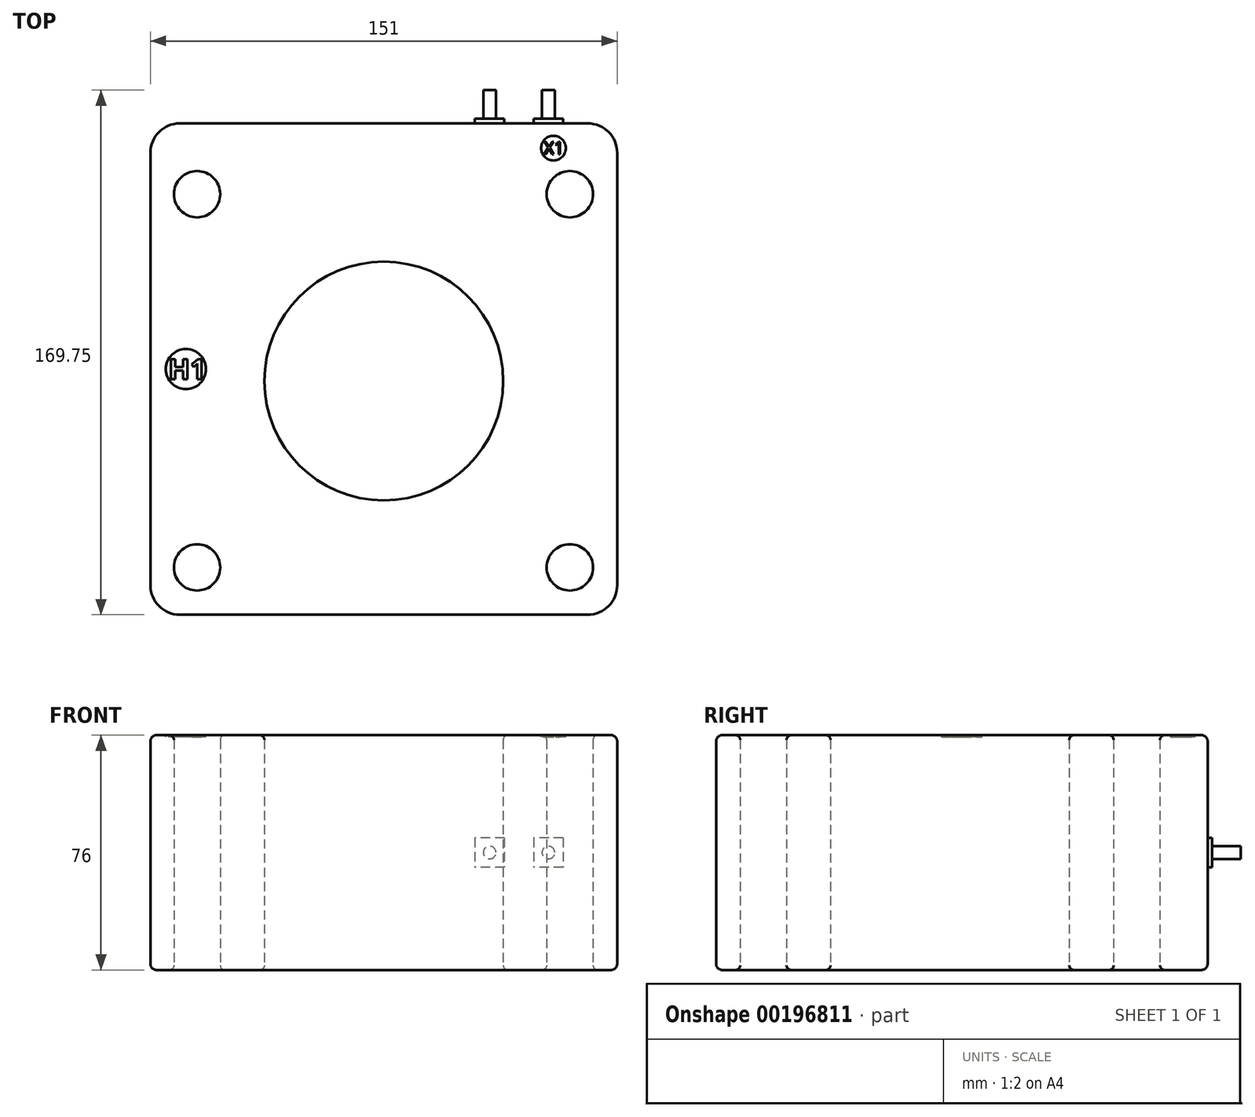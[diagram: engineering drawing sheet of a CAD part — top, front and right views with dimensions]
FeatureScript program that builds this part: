
annotation { "Feature Type Name" : "Feature", "Feature Type Description" : "" }
export const myFeature = defineFeature(function(context is Context, id is Id, definition is map)
    precondition{}
    {
        {
            var Q0;
            Q0=qCreatedBy(makeId("Top.planeOp"),FACE);
            var sketch = newSketch(context, id + "F0", { "sketchPlane" : qUnion([Q0])});
            skLineSegment(sketch, "E0.bottom", {"start": v(75.5, -79.5) * mm, "end": v(-75.5, -79.5) * mm});
            skLineSegment(sketch, "E0.top", {"start": v(75.5, 79.5) * mm, "end": v(-75.5, 79.5) * mm});
            skLineSegment(sketch, "E0.left", {"start": v(75.5, -79.5) * mm, "end": v(75.5, 79.5) * mm});
            skLineSegment(sketch, "E0.right", {"start": v(-75.5, -79.5) * mm, "end": v(-75.5, 79.5) * mm});
            skPoint(sketch, "E0.middle", {"position": v(0, 0) * mm});
            skCircle(sketch, "E1", {"center": v(0, -3.88) * mm, "radius": 38.62 * mm});
            skCircle(sketch, "E2", {"center": v(-60.4, 56.6) * mm, "radius": 7.5 * mm});
            skCircle(sketch, "E3", {"center": v(60.2, 56.6) * mm, "radius": 7.5 * mm});
            skCircle(sketch, "E4", {"center": v(-60.4, -64.2) * mm, "radius": 7.5 * mm});
            skCircle(sketch, "E5", {"center": v(60.2, -64.2) * mm, "radius": 7.5 * mm});
            skSolve(sketch);
        }
        {
            var Q0;
            Q0=makeQuery(id+"F0.imprint","IMPRINT",FACE,{"disambiguationData":[TD([[makeQuery(id+"F0.imprint","IMPRINT",EDGE,{"derivedFrom":sQuery(id+"F0.wireOp",EDGE,"E0.bottom")}),-1.0]])]});
            extrude(context, id + "F1", {"entities" : qUnion([Q0]), "depth" : 76 * mm});
        }
        {
            var Q0;
            Q0=makeQuery(id+"F1.opExtrude","SWEPT_FACE",FACE,{"disambiguationData":[OSD([sQuery(id+"F0.wireOp",EDGE,"E0.top")])]});
            var sketch = newSketch(context, id + "F2", { "sketchPlane" : qUnion([Q0])});
            skLineSegment(sketch, "E6.bottom", {"start": v(-39, 42.75) * mm, "end": v(-29.5, 42.75) * mm});
            skLineSegment(sketch, "E6.top", {"start": v(-39, 33.25) * mm, "end": v(-29.5, 33.25) * mm});
            skLineSegment(sketch, "E6.left", {"start": v(-39, 42.75) * mm, "end": v(-39, 33.25) * mm});
            skLineSegment(sketch, "E6.right", {"start": v(-29.5, 42.75) * mm, "end": v(-29.5, 33.25) * mm});
            skPoint(sketch, "E6.middle", {"position": v(-34.25, 38) * mm});
            skPoint(sketch, "E6.middle.positionSnap0", {"position": v(-75.5, 38) * mm});
            skPoint(sketch, "E6.centerSnap0", {"position": v(-75.5, 38) * mm});
            skLineSegment(sketch, "E7.bottom", {"start": v(-58, 42.75) * mm, "end": v(-48.5, 42.75) * mm});
            skLineSegment(sketch, "E7.top", {"start": v(-58, 33.25) * mm, "end": v(-48.5, 33.25) * mm});
            skLineSegment(sketch, "E7.left", {"start": v(-58, 42.75) * mm, "end": v(-58, 33.25) * mm});
            skLineSegment(sketch, "E7.right", {"start": v(-48.5, 42.75) * mm, "end": v(-48.5, 33.25) * mm});
            skPoint(sketch, "E7.middle", {"position": v(-53.25, 38) * mm});
            skSolve(sketch);
        }
        {
            var Q0;
            Q0=makeQuery(id+"F2.imprint","IMPRINT",FACE,{"disambiguationData":[TD([[makeQuery(id+"F2.imprint","IMPRINT",EDGE,{"derivedFrom":sQuery(id+"F2.wireOp",EDGE,"E6.bottom")}),-1.0]])]});
            var Q1;
            Q1=makeQuery(id+"F2.imprint","IMPRINT",FACE,{"disambiguationData":[TD([[makeQuery(id+"F2.imprint","IMPRINT",EDGE,{"derivedFrom":sQuery(id+"F2.wireOp",EDGE,"E7.bottom")}),-1.0]])]});
            extrude(context, id + "F3", {"entities" : qUnion([Q0, Q1]), "operationType" : NewBodyOperationType.ADD, "depth" : 1.5 * mm});
        }
        {
            var Q0;
            Q0=makeQuery(id+"F3.opExtrude","CAP_FACE",FACE,{"disambiguationData":[OSD([sQuery(id+"F2.wireOp",EDGE,"E6.bottom"),sQuery(id+"F2.wireOp",EDGE,"E6.top"),sQuery(id+"F2.wireOp",EDGE,"E6.left"),sQuery(id+"F2.wireOp",EDGE,"E6.right")])],"isStart":false});
            var sketch = newSketch(context, id + "F4", { "sketchPlane" : qUnion([Q0])});
            skCircle(sketch, "E8", {"center": v(-34.25, 38) * mm, "radius": 2.05 * mm});
            skPoint(sketch, "E8.centerSnap0", {"position": v(-34.25, 33.25) * mm});
            skPoint(sketch, "E8.centerSnap1", {"position": v(-39, 38) * mm});
            skSolve(sketch);
        }
        {
            var Q0;
            Q0=makeQuery(id+"F3.opExtrude","CAP_FACE",FACE,{"disambiguationData":[OSD([sQuery(id+"F2.wireOp",EDGE,"E7.bottom"),sQuery(id+"F2.wireOp",EDGE,"E7.top"),sQuery(id+"F2.wireOp",EDGE,"E7.left"),sQuery(id+"F2.wireOp",EDGE,"E7.right")])],"isStart":false});
            var sketch = newSketch(context, id + "F5", { "sketchPlane" : qUnion([Q0])});
            skCircle(sketch, "E9", {"center": v(-53.25, 38) * mm, "radius": 2.05 * mm});
            skPoint(sketch, "E9.centerSnap0", {"position": v(-58, 38) * mm});
            skPoint(sketch, "E9.centerSnap1", {"position": v(-53.25, 33.25) * mm});
            skSolve(sketch);
        }
        {
            var Q0;
            Q0=makeQuery(id+"F4.imprint","IMPRINT",FACE,{"disambiguationData":[TD([[makeQuery(id+"F4.imprint","IMPRINT",EDGE,{"derivedFrom":sQuery(id+"F4.wireOp",EDGE,"E8")}),1.0]])]});
            var Q1;
            Q1=makeQuery(id+"F5.imprint","IMPRINT",FACE,{"disambiguationData":[TD([[makeQuery(id+"F5.imprint","IMPRINT",EDGE,{"derivedFrom":sQuery(id+"F5.wireOp",EDGE,"E9")}),1.0]])]});
            extrude(context, id + "F6", {"entities" : qUnion([Q0, Q1]), "operationType" : NewBodyOperationType.ADD, "depth" : 9.25 * mm});
        }
        {
            var Q0;
            Q0=makeQuery(id+"F1.opExtrude","CAP_FACE",FACE,{"disambiguationData":[OSD([sQuery(id+"F0.wireOp",EDGE,"E0.bottom"),sQuery(id+"F0.wireOp",EDGE,"E0.top"),sQuery(id+"F0.wireOp",EDGE,"E0.left"),sQuery(id+"F0.wireOp",EDGE,"E0.right"),sQuery(id+"F0.wireOp",EDGE,"E1"),sQuery(id+"F0.wireOp",EDGE,"E2"),sQuery(id+"F0.wireOp",EDGE,"E3"),sQuery(id+"F0.wireOp",EDGE,"E4"),sQuery(id+"F0.wireOp",EDGE,"E5")])],"isStart":false});
            var sketch = newSketch(context, id + "F7", { "sketchPlane" : qUnion([Q0])});
            skCircle(sketch, "E10", {"center": v(-64, 0) * mm, "radius": 6.5 * mm});
            skPoint(sketch, "E10.centerSnap0", {"position": v(-75.5, 0) * mm});
            skCircle(sketch, "E11", {"center": v(54.9, 71.5) * mm, "radius": 4 * mm});
            skSolve(sketch);
        }
        {
            var Q0;
            Q0=makeQuery(id+"F7.imprint","IMPRINT",FACE,{"disambiguationData":[TD([[makeQuery(id+"F7.imprint","IMPRINT",EDGE,{"derivedFrom":sQuery(id+"F7.wireOp",EDGE,"E10")}),1.0]])]});
            var Q1;
            Q1=makeQuery(id+"F7.imprint","IMPRINT",FACE,{"disambiguationData":[TD([[makeQuery(id+"F7.imprint","IMPRINT",EDGE,{"derivedFrom":sQuery(id+"F7.wireOp",EDGE,"E11")}),1.0]])]});
            extrude(context, id + "F8", {"entities" : qUnion([Q0, Q1]), "operationType" : NewBodyOperationType.REMOVE, "oppositeDirection" : true, "depth" : 0.6 * mm});
        }
        {
            var Q0;
            Q0=makeQuery(id+"F8.boolean.opBoolean","COPY",FACE,{"derivedFrom":makeQuery(id+"F8.opExtrude","CAP_FACE",FACE,{"disambiguationData":[OSD([sQuery(id+"F7.wireOp",EDGE,"E10")])],"isStart":false})});
            var sketch = newSketch(context, id + "F9", { "sketchPlane" : qUnion([Q0])});
            skText(sketch, "E12", { "text": "H1", "fontName": "OpenSans-Bold.ttf"});
            const initialGuessF9  = {"E12": [-0.06964, -0.00329, 1, 0, 0.00652]};
            skSetInitialGuess(sketch, initialGuessF9);
            skSolve(sketch);
        }
        {
            var Q0;
            Q0=makeQuery(id+"F9.imprint","IMPRINT",FACE,{"disambiguationData":[TD([[makeQuery(id+"F9.imprint","IMPRINT",EDGE,{"derivedFrom":sQuery(id+"F9.wireOp",EDGE,"E12.sketch_text.stroke-0")}),-1.0]])]});
            var Q1;
            Q1=makeQuery(id+"F9.imprint","IMPRINT",FACE,{"disambiguationData":[TD([[makeQuery(id+"F9.imprint","IMPRINT",EDGE,{"derivedFrom":sQuery(id+"F9.wireOp",EDGE,"E12.sketch_text.stroke-12")}),-1.0]])]});
            extrude(context, id + "F10", {"entities" : qUnion([Q0, Q1]), "operationType" : NewBodyOperationType.ADD, "depth" : .2 * mm});
        }
        {
            var Q0;
            Q0=makeQuery(id+"F8.boolean.opBoolean","COPY",FACE,{"derivedFrom":makeQuery(id+"F8.opExtrude","CAP_FACE",FACE,{"disambiguationData":[OSD([sQuery(id+"F7.wireOp",EDGE,"E11")])],"isStart":false})});
            var sketch = newSketch(context, id + "F11", { "sketchPlane" : qUnion([Q0])});
            skText(sketch, "E13", { "text": "X1", "fontName": "OpenSans-Regular.ttf"});
            const initialGuessF11  = {"E13": [0.05177, 0.06952, 1, 0, 0.00408]};
            skSetInitialGuess(sketch, initialGuessF11);
            skSolve(sketch);
        }
        {
            var Q0;
            Q0=makeQuery(id+"F11.imprint","IMPRINT",FACE,{"disambiguationData":[TD([[makeQuery(id+"F11.imprint","IMPRINT",EDGE,{"derivedFrom":sQuery(id+"F11.wireOp",EDGE,"E13.sketch_text.stroke-0")}),-1.0]])]});
            var Q1;
            Q1=makeQuery(id+"F11.imprint","IMPRINT",FACE,{"disambiguationData":[TD([[makeQuery(id+"F11.imprint","IMPRINT",EDGE,{"derivedFrom":sQuery(id+"F11.wireOp",EDGE,"E13.sketch_text.stroke-12")}),-1.0]])]});
            extrude(context, id + "F12", {"entities" : qUnion([Q0, Q1]), "operationType" : NewBodyOperationType.ADD, "depth" : .2 * mm});
        }
        {
            var Q0;
            Q0=makeQuery(id+"F1.opExtrude","CAP_EDGE",EDGE,{"disambiguationData":[OSD([sQuery(id+"F0.wireOp",EDGE,"E0.top")])],"isStart":false});
            var Q1;
            Q1=makeQuery(id+"F1.opExtrude","CAP_EDGE",EDGE,{"disambiguationData":[OSD([sQuery(id+"F0.wireOp",EDGE,"E0.top")])],"isStart":true});
            var Q2;
            Q2=makeQuery(id+"F1.opExtrude","CAP_EDGE",EDGE,{"disambiguationData":[OSD([sQuery(id+"F0.wireOp",EDGE,"E0.left")])],"isStart":false});
            var Q3;
            Q3=makeQuery(id+"F1.opExtrude","CAP_EDGE",EDGE,{"disambiguationData":[OSD([sQuery(id+"F0.wireOp",EDGE,"E0.bottom")])],"isStart":false});
            var Q4;
            Q4=makeQuery(id+"F1.opExtrude","CAP_EDGE",EDGE,{"disambiguationData":[OSD([sQuery(id+"F0.wireOp",EDGE,"E0.right")])],"isStart":false});
            var Q5;
            Q5=makeQuery(id+"F1.opExtrude","CAP_EDGE",EDGE,{"disambiguationData":[OSD([sQuery(id+"F0.wireOp",EDGE,"E0.left")])],"isStart":true});
            var Q6;
            Q6=makeQuery(id+"F1.opExtrude","CAP_EDGE",EDGE,{"disambiguationData":[OSD([sQuery(id+"F0.wireOp",EDGE,"E0.bottom")])],"isStart":true});
            var Q7;
            Q7=makeQuery(id+"F1.opExtrude","CAP_EDGE",EDGE,{"disambiguationData":[OSD([sQuery(id+"F0.wireOp",EDGE,"E0.right")])],"isStart":true});
            fillet(context, id + "F13", {"entities" : qUnion([Q0, Q1, Q2, Q3, Q4, Q5, Q6, Q7]), "radius" : 2 * mm, "tangentPropagation" : true, "allowEdgeOverflow" : false});
        }
        {
            var Q0;
            Q0=makeQuery(id+"F1.opExtrude","SWEPT_EDGE",EDGE,{"disambiguationData":[OSD([sQuery(id+"F0.wireOp",EDGE,"E0.top"),sQuery(id+"F0.wireOp",EDGE,"E0.left")])]});
            var Q1;
            Q1=makeQuery(id+"F1.opExtrude","SWEPT_EDGE",EDGE,{"disambiguationData":[OSD([sQuery(id+"F0.wireOp",EDGE,"E0.top"),sQuery(id+"F0.wireOp",EDGE,"E0.right")])]});
            var Q2;
            Q2=makeQuery(id+"F1.opExtrude","SWEPT_EDGE",EDGE,{"disambiguationData":[OSD([sQuery(id+"F0.wireOp",EDGE,"E0.bottom"),sQuery(id+"F0.wireOp",EDGE,"E0.right")])]});
            var Q3;
            Q3=makeQuery(id+"F1.opExtrude","SWEPT_EDGE",EDGE,{"disambiguationData":[OSD([sQuery(id+"F0.wireOp",EDGE,"E0.bottom"),sQuery(id+"F0.wireOp",EDGE,"E0.left")])]});
            fillet(context, id + "F14", {"entities" : qUnion([Q0, Q1, Q2, Q3]), "radius" : 9.5 * mm, "tangentPropagation" : true, "allowEdgeOverflow" : false});
        }
        {
            var Q0;
            Q0=makeQuery(id+"F1.opExtrude","CAP_EDGE",EDGE,{"disambiguationData":[OSD([sQuery(id+"F0.wireOp",EDGE,"E3")])],"isStart":true});
            var Q1;
            Q1=makeQuery(id+"F1.opExtrude","CAP_EDGE",EDGE,{"disambiguationData":[OSD([sQuery(id+"F0.wireOp",EDGE,"E5")])],"isStart":true});
            var Q2;
            Q2=makeQuery(id+"F1.opExtrude","CAP_EDGE",EDGE,{"disambiguationData":[OSD([sQuery(id+"F0.wireOp",EDGE,"E1")])],"isStart":true});
            var Q3;
            Q3=makeQuery(id+"F1.opExtrude","CAP_EDGE",EDGE,{"disambiguationData":[OSD([sQuery(id+"F0.wireOp",EDGE,"E4")])],"isStart":true});
            var Q4;
            Q4=makeQuery(id+"F1.opExtrude","CAP_EDGE",EDGE,{"disambiguationData":[OSD([sQuery(id+"F0.wireOp",EDGE,"E2")])],"isStart":true});
            var Q5;
            Q5=makeQuery(id+"F1.opExtrude","CAP_EDGE",EDGE,{"disambiguationData":[OSD([sQuery(id+"F0.wireOp",EDGE,"E1")])],"isStart":false});
            var Q6;
            Q6=makeQuery(id+"F1.opExtrude","CAP_EDGE",EDGE,{"disambiguationData":[OSD([sQuery(id+"F0.wireOp",EDGE,"E3")])],"isStart":false});
            var Q7;
            Q7=makeQuery(id+"F1.opExtrude","CAP_EDGE",EDGE,{"disambiguationData":[OSD([sQuery(id+"F0.wireOp",EDGE,"E2")])],"isStart":false});
            var Q8;
            Q8=makeQuery(id+"F1.opExtrude","CAP_EDGE",EDGE,{"disambiguationData":[OSD([sQuery(id+"F0.wireOp",EDGE,"E4")])],"isStart":false});
            var Q9;
            Q9=makeQuery(id+"F1.opExtrude","CAP_EDGE",EDGE,{"disambiguationData":[OSD([sQuery(id+"F0.wireOp",EDGE,"E5")])],"isStart":false});
            fillet(context, id + "F15", {"entities" : qUnion([Q0, Q1, Q2, Q3, Q4, Q5, Q6, Q7, Q8, Q9]), "radius" : 1.5 * mm, "tangentPropagation" : true, "allowEdgeOverflow" : false});
        }
    });
